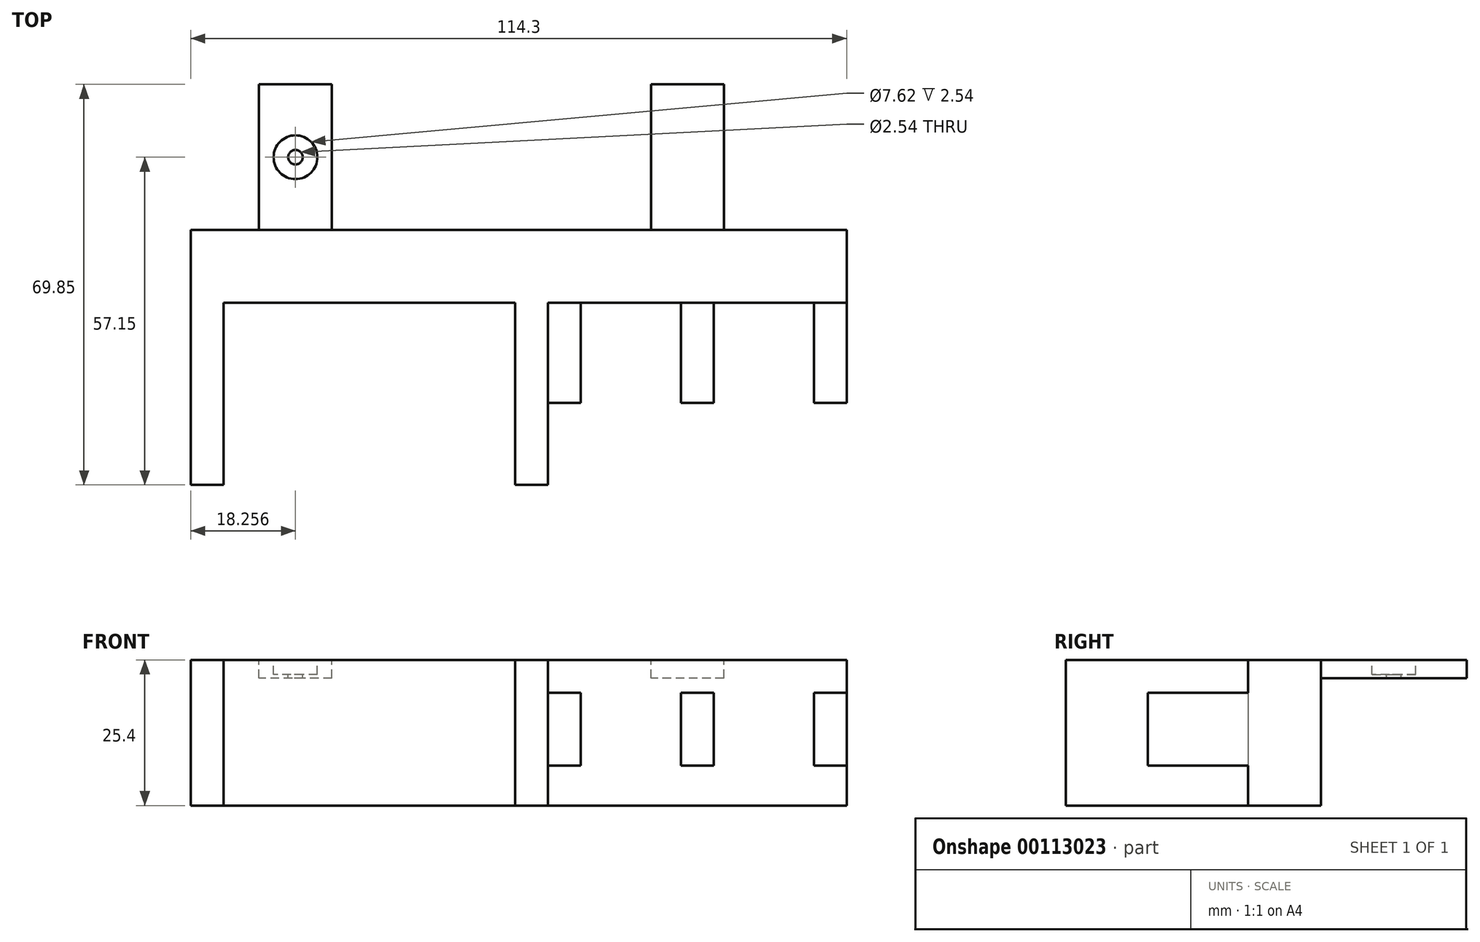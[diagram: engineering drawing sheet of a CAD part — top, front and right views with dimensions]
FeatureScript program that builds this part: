
annotation { "Feature Type Name" : "Feature", "Feature Type Description" : "" }
export const myFeature = defineFeature(function(context is Context, id is Id, definition is map)
    precondition{}
    {
        {
            var Q0;
            Q0=qCreatedBy(makeId("Front.planeOp"),FACE);
            var sketch = newSketch(context, id + "F0", { "sketchPlane" : qUnion([Q0])});
            skLineSegment(sketch, "E0", {"start": v(-76.76, 0) * mm, "end": v(37.54, 0) * mm});
            skLineSegment(sketch, "E1", {"start": v(37.54, 0) * mm, "end": v(37.54, 25.4) * mm});
            skLineSegment(sketch, "E2", {"start": v(37.54, 25.4) * mm, "end": v(-76.76, 25.4) * mm});
            skLineSegment(sketch, "E3", {"start": v(-76.76, 25.4) * mm, "end": v(-76.76, 0) * mm});
            skSolve(sketch);
        }
        {
            var Q0;
            Q0=makeQuery(id+"F0.imprint","IMPRINT",FACE,{"disambiguationData":[TD([[makeQuery(id+"F0.imprint","IMPRINT",EDGE,{"derivedFrom":sQuery(id+"F0.wireOp",EDGE,"E0")}),1.0]])]});
            extrude(context, id + "F1", {"entities" : qUnion([Q0]), "oppositeDirection" : true, "depth" : 12.7 * mm});
        }
        {
            var Q0;
            Q0=makeQuery(id+"F1.opExtrude","CAP_FACE",FACE,{"disambiguationData":[OSD([sQuery(id+"F0.wireOp",EDGE,"E0"),sQuery(id+"F0.wireOp",EDGE,"E1"),sQuery(id+"F0.wireOp",EDGE,"E2"),sQuery(id+"F0.wireOp",EDGE,"E3")])],"isStart":true});
            var sketch = newSketch(context, id + "F2", { "sketchPlane" : qUnion([Q0])});
            skLineSegment(sketch, "E4.bottom", {"start": v(-20.24, 25.4) * mm, "end": v(-14.53, 25.4) * mm});
            skLineSegment(sketch, "E4.top", {"start": v(-20.24, 0) * mm, "end": v(-14.53, 0) * mm});
            skLineSegment(sketch, "E4.left", {"start": v(-20.24, 25.4) * mm, "end": v(-20.24, 0) * mm});
            skLineSegment(sketch, "E4.right", {"start": v(-14.53, 25.4) * mm, "end": v(-14.53, 0) * mm});
            skLineSegment(sketch, "E5.bottom", {"start": v(-76.76, 25.4) * mm, "end": v(-71.04, 25.4) * mm});
            skLineSegment(sketch, "E5.top", {"start": v(-76.76, 0) * mm, "end": v(-71.04, 0) * mm});
            skLineSegment(sketch, "E5.left", {"start": v(-76.76, 25.4) * mm, "end": v(-76.76, 0) * mm});
            skLineSegment(sketch, "E5.right", {"start": v(-71.04, 25.4) * mm, "end": v(-71.04, 0) * mm});
            skLineSegment(sketch, "E6.bottom", {"start": v(-14.53, 19.05) * mm, "end": v(-8.81, 19.05) * mm});
            skLineSegment(sketch, "E6.top", {"start": v(-14.53, 6.35) * mm, "end": v(-8.81, 6.35) * mm});
            skLineSegment(sketch, "E6.left", {"start": v(-14.53, 19.05) * mm, "end": v(-14.53, 6.35) * mm});
            skLineSegment(sketch, "E6.right", {"start": v(-8.81, 19.05) * mm, "end": v(-8.81, 6.35) * mm});
            skLineSegment(sketch, "E7.bottom", {"start": v(8.65, 19.05) * mm, "end": v(14.36, 19.05) * mm});
            skLineSegment(sketch, "E7.top", {"start": v(8.65, 6.35) * mm, "end": v(14.36, 6.35) * mm});
            skLineSegment(sketch, "E7.left", {"start": v(8.65, 19.05) * mm, "end": v(8.65, 6.35) * mm});
            skLineSegment(sketch, "E7.right", {"start": v(14.36, 19.05) * mm, "end": v(14.36, 6.35) * mm});
            skLineSegment(sketch, "E8.bottom", {"start": v(31.83, 19.05) * mm, "end": v(37.54, 19.05) * mm});
            skLineSegment(sketch, "E8.top", {"start": v(31.83, 6.35) * mm, "end": v(37.54, 6.35) * mm});
            skLineSegment(sketch, "E8.left", {"start": v(31.83, 19.05) * mm, "end": v(31.83, 6.35) * mm});
            skLineSegment(sketch, "E8.right", {"start": v(37.54, 19.05) * mm, "end": v(37.54, 6.35) * mm});
            skSolve(sketch);
        }
        {
            var Q0;
            Q0=makeQuery(id+"F2.imprint","IMPRINT",FACE,{"disambiguationData":[TD([[makeQuery(id+"F2.imprint","IMPRINT",EDGE,{"derivedFrom":sQuery(id+"F2.wireOp",EDGE,"E5.bottom")}),1.0]])]});
            var Q1;
            {var subQ1=sQuery(id+"F2.wireOp",EDGE,"E4.bottom");Q1=makeQuery(id+"F2.imprint","IMPRINT",FACE,{"disambiguationData":[TD([[makeQuery(id+"F2.imprint","IMPRINT",EDGE,{"derivedFrom":subQ1}),1.0]])]});}
            extrude(context, id + "F3", {"entities" : qUnion([Q0, Q1]), "operationType" : NewBodyOperationType.ADD, "depth" : 31.75 * mm});
        }
        {
            var Q0;
            {var subQ0=sQuery(id+"F0.wireOp",EDGE,"E2");var subQ1=sQuery(id+"F0.wireOp",EDGE,"E1");var subQ2=sQuery(id+"F0.wireOp",EDGE,"E0");Q0=makeQuery(id+"F3.boolean.opBoolean","SPLIT",FACE,{"disambiguationData":[TD([makeQuery(id+"F1.opExtrude","SWEPT_FACE",FACE,{"disambiguationData":[OSD([subQ1])]})])],"derivedFrom":makeQuery(id+"F1.opExtrude","CAP_FACE",FACE,{"disambiguationData":[OSD([subQ2,subQ1,subQ0,sQuery(id+"F0.wireOp",EDGE,"E3")])],"isStart":true})});}
            var sketch = newSketch(context, id + "F4", { "sketchPlane" : qUnion([Q0])});
            skLineSegment(sketch, "E9.bottom", {"start": v(-14.53, 19.66) * mm, "end": v(-8.81, 19.66) * mm});
            skLineSegment(sketch, "E9.top", {"start": v(-14.53, 6.96) * mm, "end": v(-8.81, 6.96) * mm});
            skLineSegment(sketch, "E9.left", {"start": v(-14.53, 19.66) * mm, "end": v(-14.53, 6.96) * mm});
            skLineSegment(sketch, "E9.right", {"start": v(-8.81, 19.66) * mm, "end": v(-8.81, 6.96) * mm});
            skPoint(sketch, "E10.firstSnap0", {"position": v(-11.67, 19.66) * mm});
            skLineSegment(sketch, "E10.bottom", {"start": v(8.65, 19.66) * mm, "end": v(14.36, 19.66) * mm});
            skLineSegment(sketch, "E10.top", {"start": v(8.65, 6.96) * mm, "end": v(14.36, 6.96) * mm});
            skLineSegment(sketch, "E10.left", {"start": v(8.65, 19.66) * mm, "end": v(8.65, 6.96) * mm});
            skLineSegment(sketch, "E10.right", {"start": v(14.36, 19.66) * mm, "end": v(14.36, 6.96) * mm});
            skLineSegment(sketch, "E11.bottom", {"start": v(37.54, 19.66) * mm, "end": v(31.83, 19.66) * mm});
            skLineSegment(sketch, "E11.top", {"start": v(37.54, 6.96) * mm, "end": v(31.83, 6.96) * mm});
            skLineSegment(sketch, "E11.left", {"start": v(37.54, 19.66) * mm, "end": v(37.54, 6.96) * mm});
            skLineSegment(sketch, "E11.right", {"start": v(31.83, 19.66) * mm, "end": v(31.83, 6.96) * mm});
            skSolve(sketch);
        }
        {
            var Q0;
            Q0 = qSketchRegion(id + "F4", true);
            extrude(context, id + "F5", {"entities" : qUnion([Q0]), "operationType" : NewBodyOperationType.ADD, "depth" : 17.46 * mm});
        }
        {
            var Q0;
            Q0=makeQuery(id+"F3.boolean.opBoolean","MERGE",FACE,{"derivedFrom":[makeQuery(id+"F1.opExtrude","SWEPT_FACE",FACE,{"disambiguationData":[OSD([sQuery(id+"F0.wireOp",EDGE,"E2")])]}),makeQuery(id+"F3.opExtrude","SWEPT_FACE",FACE,{"disambiguationData":[OSD([sQuery(id+"F2.wireOp",EDGE,"E4.bottom")])]}),makeQuery(id+"F3.opExtrude","SWEPT_FACE",FACE,{"disambiguationData":[OSD([sQuery(id+"F2.wireOp",EDGE,"E5.bottom")])]})]});
            var sketch = newSketch(context, id + "F6", { "sketchPlane" : qUnion([Q0])});
            skLineSegment(sketch, "E12", {"start": v(-64.85, 12.7) * mm, "end": v(-64.85, 38.1) * mm});
            skLineSegment(sketch, "E13", {"start": v(-64.85, 38.1) * mm, "end": v(-52.15, 38.1) * mm});
            skLineSegment(sketch, "E14", {"start": v(-52.15, 38.1) * mm, "end": v(-52.15, 12.7) * mm});
            skLineSegment(sketch, "E15", {"start": v(3.45, 12.7) * mm, "end": v(3.45, 38.1) * mm});
            skLineSegment(sketch, "E16", {"start": v(3.45, 38.1) * mm, "end": v(16.15, 38.1) * mm});
            skLineSegment(sketch, "E17", {"start": v(16.15, 38.1) * mm, "end": v(16.15, 12.7) * mm});
            skSolve(sketch);
        }
        {
            var Q0;
            {var subQ0=sQuery(id+"F6.wireOp",EDGE,"E12");Q0=makeQuery(id+"F6.imprint","IMPRINT",FACE,{"disambiguationData":[TD([[makeQuery(id+"F6.imprint","IMPRINT",EDGE,{"derivedFrom":subQ0}),-1.0]])]});}
            var Q1;
            {var subQ0=sQuery(id+"F6.wireOp",EDGE,"E15");Q1=makeQuery(id+"F6.imprint","IMPRINT",FACE,{"disambiguationData":[TD([[makeQuery(id+"F6.imprint","IMPRINT",EDGE,{"derivedFrom":subQ0}),-1.0]])]});}
            extrude(context, id + "F7", {"entities" : qUnion([Q0, Q1]), "oppositeDirection" : true, "depth" : 3.17 * mm});
        }
        {
            var Q0;
            Q0=makeQuery(id+"F7.opExtrude","CAP_FACE",FACE,{"disambiguationData":[OSD([sQuery(id+"F0.wireOp",EDGE,"E2"),sQuery(id+"F6.wireOp",EDGE,"E12"),sQuery(id+"F6.wireOp",EDGE,"E13"),sQuery(id+"F6.wireOp",EDGE,"E14")])],"isStart":true});
            var sketch = newSketch(context, id + "F8", { "sketchPlane" : qUnion([Q0])});
            skCircle(sketch, "E18", {"center": v(-58.5, 25.4) * mm, "radius": 3.81 * mm});
            skPoint(sketch, "E18.centerSnap0", {"position": v(-64.85, 25.4) * mm});
            skPoint(sketch, "E18.centerSnap1", {"position": v(-58.5, 38.1) * mm});
            skSolve(sketch);
        }
        {
            var Q0;
            Q0 = qSketchRegion(id + "F8", true);
            extrude(context, id + "F9", {"entities" : qUnion([Q0]), "operationType" : NewBodyOperationType.REMOVE, "oppositeDirection" : true, "depth" : 2.54 * mm});
        }
        {
            var Q0;
            Q0=makeQuery(id+"F9.boolean.opBoolean","COPY",FACE,{"derivedFrom":makeQuery(id+"F9.opExtrude","CAP_FACE",FACE,{"disambiguationData":[OSD([sQuery(id+"F8.wireOp",EDGE,"E18")])],"isStart":false})});
            var sketch = newSketch(context, id + "F10", { "sketchPlane" : qUnion([Q0])});
            skCircle(sketch, "E19", {"center": v(-58.5, 25.4) * mm, "radius": 1.27 * mm});
            skSolve(sketch);
        }
        {
            var Q0;
            Q0 = qSketchRegion(id + "F10", true);
            extrude(context, id + "F11", {"entities" : qUnion([Q0]), "operationType" : NewBodyOperationType.REMOVE, "endBound" : BoundingType.THROUGH_ALL, "oppositeDirection" : true, "depth" : 25.4 * mm});
        }
    });
